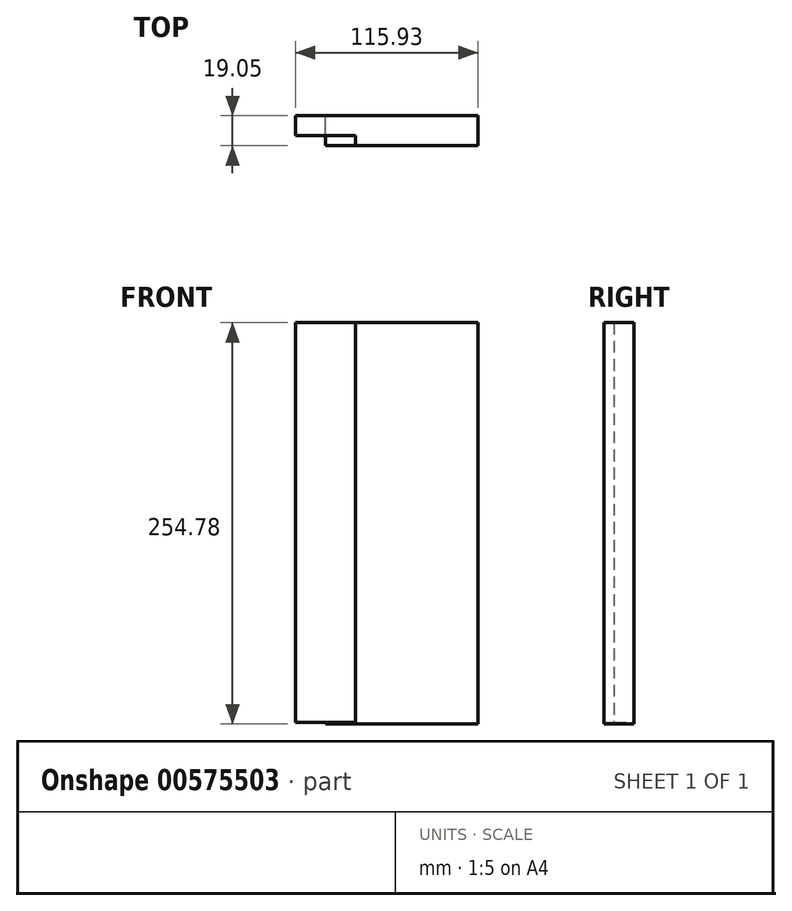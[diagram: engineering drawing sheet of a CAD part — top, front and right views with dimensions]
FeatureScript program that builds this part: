
annotation { "Feature Type Name" : "Feature", "Feature Type Description" : "" }
export const myFeature = defineFeature(function(context is Context, id is Id, definition is map)
    precondition{}
    {
        {
            var Q0;
            Q0=qCreatedBy(makeId("Front.planeOp"),FACE);
            var sketch = newSketch(context, id + "F0", { "sketchPlane" : qUnion([Q0])});
            skLineSegment(sketch, "E0.bottom", {"start": v(-72.75, 123.42) * mm, "end": v(-34.65, 123.42) * mm});
            skLineSegment(sketch, "E0.top", {"start": v(-72.75, -130.58) * mm, "end": v(-34.65, -130.58) * mm});
            skLineSegment(sketch, "E0.left", {"start": v(-72.75, 123.42) * mm, "end": v(-72.75, -130.58) * mm});
            skLineSegment(sketch, "E0.right", {"start": v(-34.65, 123.42) * mm, "end": v(-34.65, -130.58) * mm});
            skLineSegment(sketch, "E1.bottom", {"start": v(-53.7, 123.42) * mm, "end": v(43.18, 123.42) * mm});
            skLineSegment(sketch, "E1.top", {"start": v(-53.7, -131.36) * mm, "end": v(43.18, -131.36) * mm});
            skLineSegment(sketch, "E1.left", {"start": v(-53.7, 123.42) * mm, "end": v(-53.7, -131.36) * mm});
            skLineSegment(sketch, "E1.right", {"start": v(43.18, 123.42) * mm, "end": v(43.18, -131.36) * mm});
            skLineSegment(sketch, "E2.bottom", {"start": v(-5.26, 123.42) * mm, "end": v(20.14, 123.42) * mm});
            skLineSegment(sketch, "E2.top", {"start": v(-5.26, 186.92) * mm, "end": v(20.14, 186.92) * mm});
            skLineSegment(sketch, "E2.left", {"start": v(-5.26, 123.42) * mm, "end": v(-5.26, 186.92) * mm});
            skLineSegment(sketch, "E2.right", {"start": v(20.14, 123.42) * mm, "end": v(20.14, 186.92) * mm});
            skSolve(sketch);
        }
        {
            var Q0;
            {var subQ1=sQuery(id+"F0.wireOp",EDGE,"E0.right");Q0=makeQuery(id+"F0.imprint","IMPRINT",FACE,{"disambiguationData":[TD([[makeQuery(id+"F0.imprint","IMPRINT",EDGE,{"derivedFrom":subQ1}),1.0]])]});}
            extrude(context, id + "F1", {"entities" : qUnion([Q0]), "depth" : 19.05 * mm, "offsetDistance" : 25.4 * mm});
        }
        {
            var Q0;
            {var subQ0=sQuery(id+"F0.wireOp",EDGE,"E0.right");Q0=makeQuery(id+"F0.imprint","IMPRINT",FACE,{"disambiguationData":[TD([[makeQuery(id+"F0.imprint","IMPRINT",EDGE,{"derivedFrom":subQ0}),-1.0]])]});}
            var Q1;
            {var subQ0=sQuery(id+"F0.wireOp",EDGE,"E0.bottom");Q1=makeQuery(id+"F0.imprint","IMPRINT",FACE,{"disambiguationData":[TD([[makeQuery(id+"F0.imprint","IMPRINT",EDGE,{"derivedFrom":subQ0}),-1.0]])]});}
            var Q2;
            Q2=makeQuery(id+"F0.imprint","IMPRINT",FACE,{"disambiguationData":[TD([[makeQuery(id+"F0.imprint","IMPRINT",EDGE,{"derivedFrom":sQuery(id+"F0.wireOp",EDGE,"E2.bottom")}),1.0]])]});
            extrude(context, id + "F2", {"entities" : qUnion([Q0, Q1, Q2]), "operationType" : NewBodyOperationType.ADD, "depth" : 12.7 * mm, "offsetDistance" : 25.4 * mm});
        }
    });
